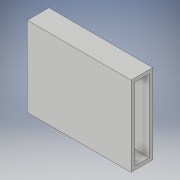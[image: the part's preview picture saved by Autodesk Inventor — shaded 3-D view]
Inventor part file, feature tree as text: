
AUTODESK INVENTOR PART (.ipt)
format: ipt  version: 2018 (Build 220112000, 112)  size: 98,304 bytes
history: native  units: in
note: dims shown in document units (in); Inventor stores cm internally (conversion verified against a paired STEP export)
features: sketch x2, extrude x2
ambient origin geometry x8: Origin, YZ Plane, XZ Plane, XY Plane, X Axis, Y Axis, Z Axis, Center Point
bodies: Solid1 (feature_tree)
feature tree (4):
  sketch  "Sketch1"  dims[d0=3.45in d1=2.5in]
  extrude  "Extrusion1"  Depth=2.5in
  extrude  "Extrusion2"  Depth=0.125in
  sketch  "Sketch2"  dims[d2=0.125in d3=0.125in d4=2.625in d6=0.0in d7=0.75in d8=0.0in d9=0.5in d10=0.0in]
